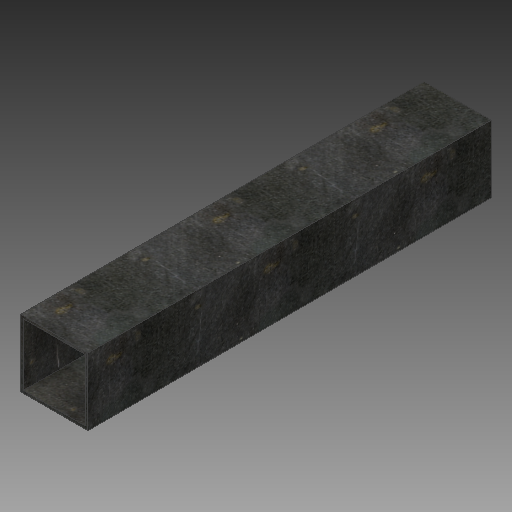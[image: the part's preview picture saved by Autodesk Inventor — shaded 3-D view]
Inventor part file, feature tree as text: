
AUTODESK INVENTOR PART (.ipt)
format: ipt  version: 2018 (Build 220112000, 112)  size: 210,432 bytes
history: native  units: mm
features: other x1, extrude x1, sketch x1
ambient origin geometry x8: Origin, YZ Plane, XZ Plane, XY Plane, X Axis, Y Axis, Z Axis, Center Point
bodies: Body1 (feature_tree)
feature tree (3):
  other  "Sólido1"
  extrude  "Extrusión1"  Depth=75.0mm
  sketch  "Boceto1"  dims[d0=75.0mm d1=75.0mm d2=3.0mm d3=37.5mm d4=37.5mm d5=450.0mm d6=0.0mm]
